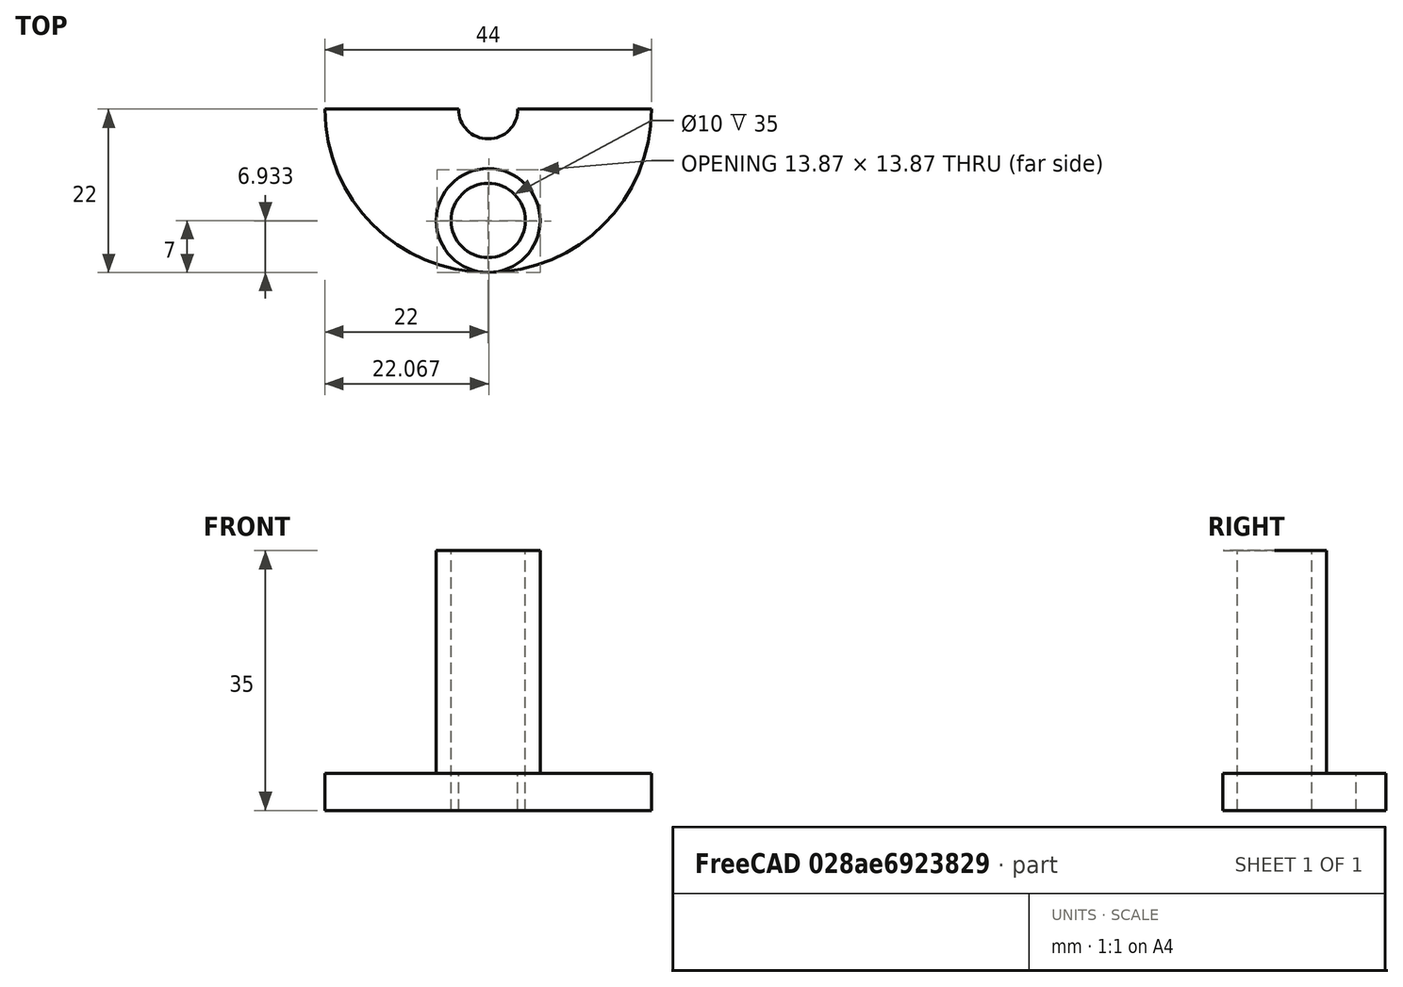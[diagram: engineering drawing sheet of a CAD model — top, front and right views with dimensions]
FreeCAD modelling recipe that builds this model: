
FCSTD DOCUMENT  (FreeCAD 0.15R4671 (Git))
Label: Pill pipe
License: CC-BY 3.0
LicenseURL: http://creativecommons.org/licenses/by/3.0/
objects: Part::Cylinder×4, Part::Cut×3, Part::MultiFuse×1, Part::Box×1
note: 9 computed .brp shape members not serialized (recipe doc carries the construction recipe); baked Part::Feature solids carry a one-line shape summary decoded from their .brp

FEATURE [Part::Cylinder] Cylinder007  label="Cilindro007"
  Angle = 360
  Height = 5
  Placement = pos=(0,0,-52) rot=(0,0,1;0rad)
  Radius = 22
FEATURE [Part::Cylinder] Cylinder008  label="Cilindro008"
  Angle = 360
  Height = 35
  Placement = pos=(0,-15,-52) rot=(0,0,1;0rad)
  Radius = 7
FEATURE [Part::Cylinder] Cylinder009  label="Cilindro009"
  Angle = 360
  Height = 55
  Placement = pos=(0,-15,-64) rot=(0,0,1;0rad)
  Radius = 5
FEATURE [Part::Cylinder] Cylinder010  label="Cilindro010"
  Angle = 360
  Height = 45
  Placement = pos=(0,0,-79) rot=(0,0,1;0rad)
  Radius = 4
FEATURE [Part::MultiFuse] Fusion
  Shapes = -> [Cylinder008,Cylinder007]
FEATURE [Part::Cut] Cut
  Base = -> Fusion
  Tool = -> Cylinder010
FEATURE [Part::Cut] Cut001
  Base = -> Cut
  Tool = -> Cylinder009
FEATURE [Part::Box] Box  label="Cubo"
  Height = 34
  Length = 30
  Placement = pos=(1,-8,-55) rot=(0,0,1;0.890118rad)
  Width = 34
FEATURE [Part::Cut] Cut002
  Base = -> Cut001
  Tool = -> Box
